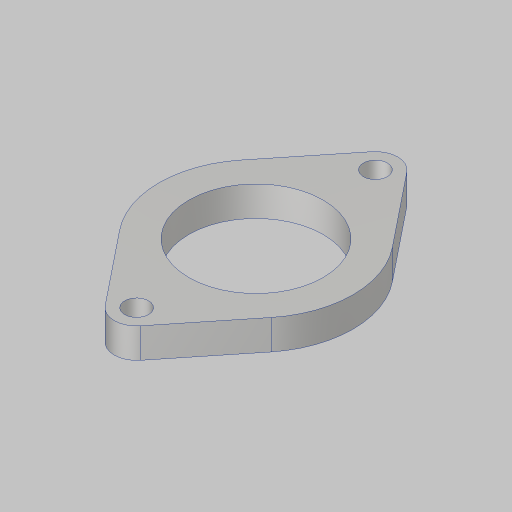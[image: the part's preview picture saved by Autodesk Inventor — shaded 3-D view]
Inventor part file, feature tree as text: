
AUTODESK INVENTOR PART (.ipt)
format: ipt  version: 2023.5 (Build 275446000, 446)  size: 115,200 bytes
history: native  units: in
note: dims shown in document units (in); Inventor stores cm internally (conversion verified against a paired STEP export)
features: sketch x1, extrude x1, hole x1
ambient origin geometry x8: Origin, YZ Plane, XZ Plane, XY Plane, X Axis, Y Axis, Z Axis, Center Point
bodies: Solid1 (feature_tree)
feature tree (3):
  sketch  "Sketch1"  dims[d0=1.125in d1=2.0in d2=1.432in d3=0.375in d4=0.375in d5=0.25in d6=0.25in d7=0.0in d8=0.201in d9=0.38in d10=0.385in d11=0.25in d12=0.5635in d13=1.0in d14=0.8108in]
  extrude  "Extrusion1"  Depth=1.0in
  hole  "Hole1"  [1 undecoded]
note: 1 required parameter value undecoded (feature->parameter linkage not recoverable at this tier; creation-order binding heuristic only, values carry confidence <= 0.55)
